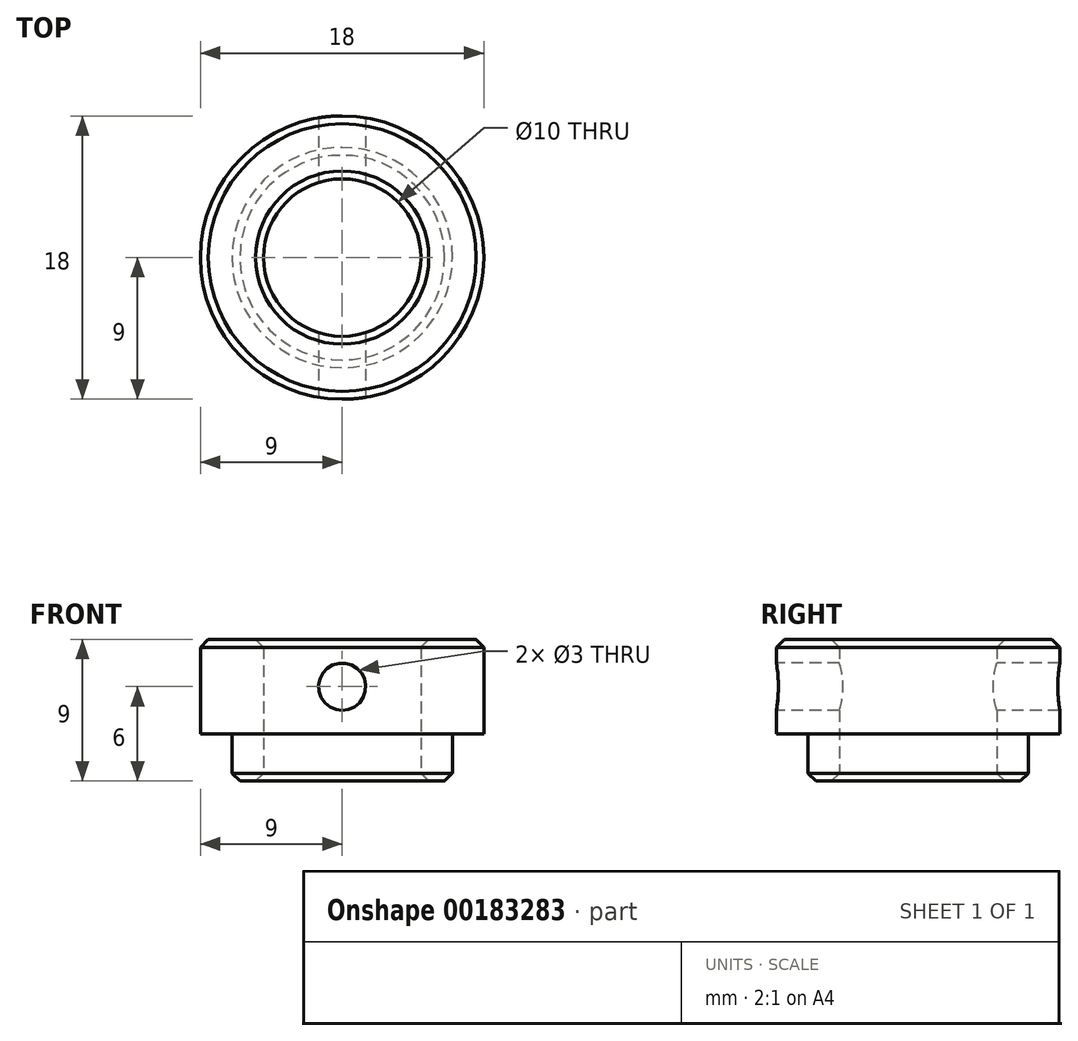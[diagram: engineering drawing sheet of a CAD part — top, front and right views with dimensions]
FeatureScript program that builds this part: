
annotation { "Feature Type Name" : "Feature", "Feature Type Description" : "" }
export const myFeature = defineFeature(function(context is Context, id is Id, definition is map)
    precondition{}
    {
        {
            var Q0;
            Q0=qCreatedBy(makeId("Top.planeOp"),FACE);
            var sketch = newSketch(context, id + "F0", { "sketchPlane" : qUnion([Q0])});
            skCircle(sketch, "E0", {"center": v(0, 0) * mm, "radius": 7 * mm});
            skCircle(sketch, "E1", {"center": v(0, 0) * mm, "radius": 5 * mm});
            skSolve(sketch);
        }
        {
            var Q0;
            Q0 = qSketchRegion(id + "F0", true);
            extrude(context, id + "F1", {"entities" : qUnion([Q0]), "depth" : 3 * mm});
        }
        {
            var Q0;
            Q0=makeQuery(id+"F1.opExtrude","CAP_FACE",FACE,{"disambiguationData":[OSD([sQuery(id+"F0.wireOp",EDGE,"E0"),sQuery(id+"F0.wireOp",EDGE,"E1")])],"isStart":false});
            var sketch = newSketch(context, id + "F2", { "sketchPlane" : qUnion([Q0])});
            skCircle(sketch, "E2.0", {"center": v(0, 0) * mm, "radius": 5 * mm});
            skCircle(sketch, "E3", {"center": v(0, 0) * mm, "radius": 9 * mm});
            skSolve(sketch);
        }
        {
            var Q0;
            Q0 = qSketchRegion(id + "F2", true);
            extrude(context, id + "F3", {"entities" : qUnion([Q0]), "operationType" : NewBodyOperationType.ADD, "depth" : 6 * mm});
        }
        {
            var Q0;
            Q0=qCreatedBy(makeId("Front.planeOp"),FACE);
            var sketch = newSketch(context, id + "F4", { "sketchPlane" : qUnion([Q0])});
            skCircle(sketch, "E4", {"center": v(0, 6) * mm, "radius": 1.5 * mm});
            skLineSegment(sketch, "E5", {"start": v(0, 9) * mm, "end": v(0, 3) * mm, "construction": true});
            skSolve(sketch);
        }
        {
            var Q0;
            Q0 = qSketchRegion(id + "F4", true);
            extrude(context, id + "F5", {"entities" : qUnion([Q0]), "operationType" : NewBodyOperationType.REMOVE, "endBound" : BoundingType.SYMMETRIC, "oppositeDirection" : true, "depth" : 25 * mm});
        }
        {
            var Q0;
            Q0=makeQuery(id+"F3.opExtrude","CAP_EDGE",EDGE,{"disambiguationData":[OSD([sQuery(id+"F2.wireOp",EDGE,"E3")])],"isStart":false});
            var Q1;
            Q1=makeQuery(id+"F1.opExtrude","CAP_EDGE",EDGE,{"disambiguationData":[OSD([sQuery(id+"F0.wireOp",EDGE,"E0")])],"isStart":true});
            var Q2;
            Q2=makeQuery(id+"F3.opExtrude","CAP_EDGE",EDGE,{"disambiguationData":[OSD([sQuery(id+"F2.wireOp",EDGE,"E2.0")])],"isStart":false});
            var Q3;
            Q3=makeQuery(id+"F1.opExtrude","CAP_EDGE",EDGE,{"disambiguationData":[OSD([sQuery(id+"F0.wireOp",EDGE,"E1")])],"isStart":true});
            chamfer(context, id + "F6", {"entities" : qUnion([Q0, Q1, Q2, Q3]), "width" : 0.5 * mm, "tangentPropagation" : true});
        }
    });
